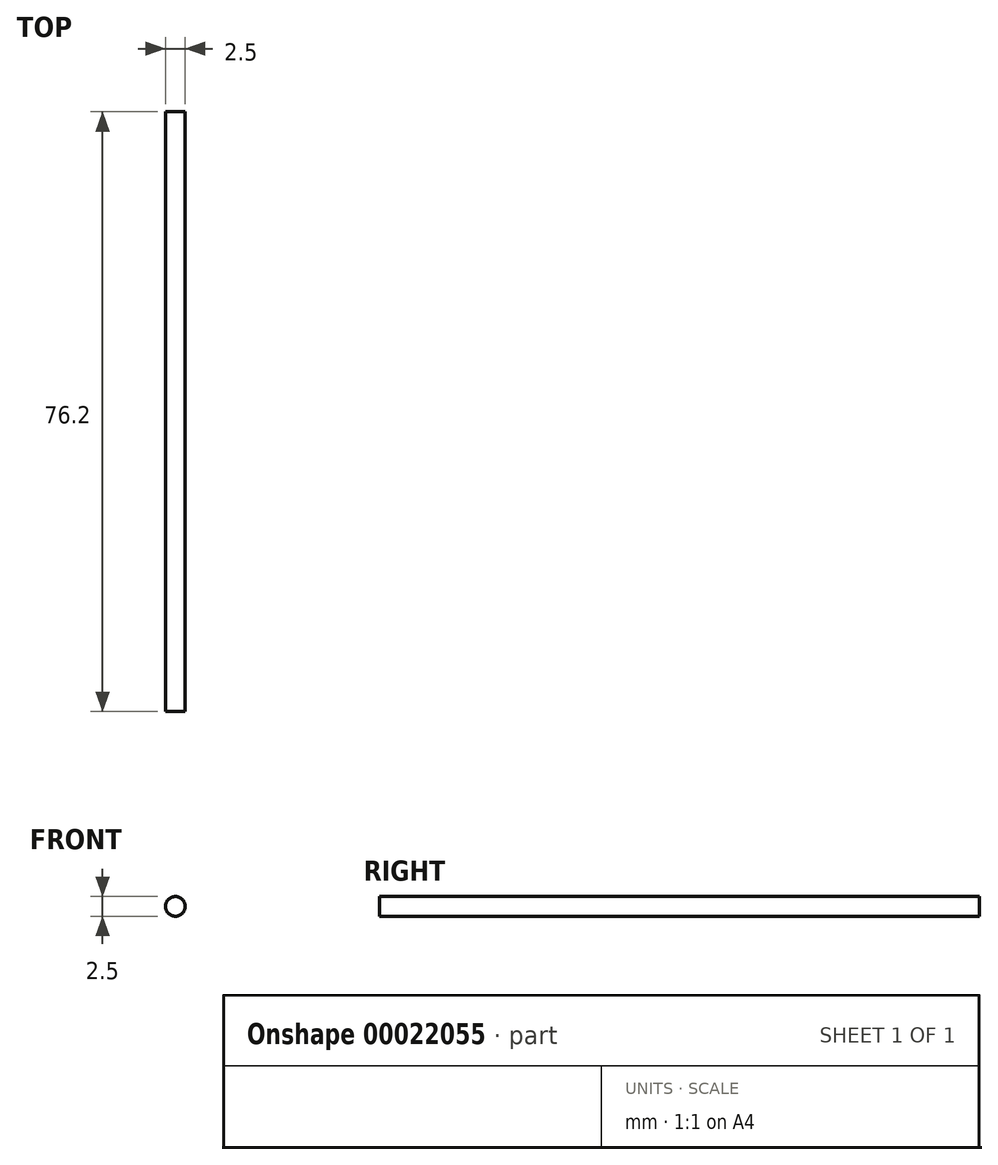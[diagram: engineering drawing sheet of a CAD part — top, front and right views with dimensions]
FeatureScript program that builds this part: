
annotation { "Feature Type Name" : "Feature", "Feature Type Description" : "" }
export const myFeature = defineFeature(function(context is Context, id is Id, definition is map)
    precondition{}
    {
        {
            var Q0;
            Q0=qCreatedBy(makeId("Front.planeOp"),FACE);
            var sketch = newSketch(context, id + "F0", { "sketchPlane" : qUnion([Q0])});
            skCircle(sketch, "E0", {"center": v(-70.62, 26) * mm, "radius": 1.25 * mm});
            skSolve(sketch);
        }
        {
            var Q0;
            Q0=makeQuery(id+"F0.imprint","IMPRINT",FACE,{"disambiguationData":[TD([[makeQuery(id+"F0.imprint","IMPRINT",EDGE,{"derivedFrom":sQuery(id+"F0.wireOp",EDGE,"E0")}),1.0]])]});
            extrude(context, id + "F1", {"entities" : qUnion([Q0]), "depth" : 76.2 * mm});
        }
    });
